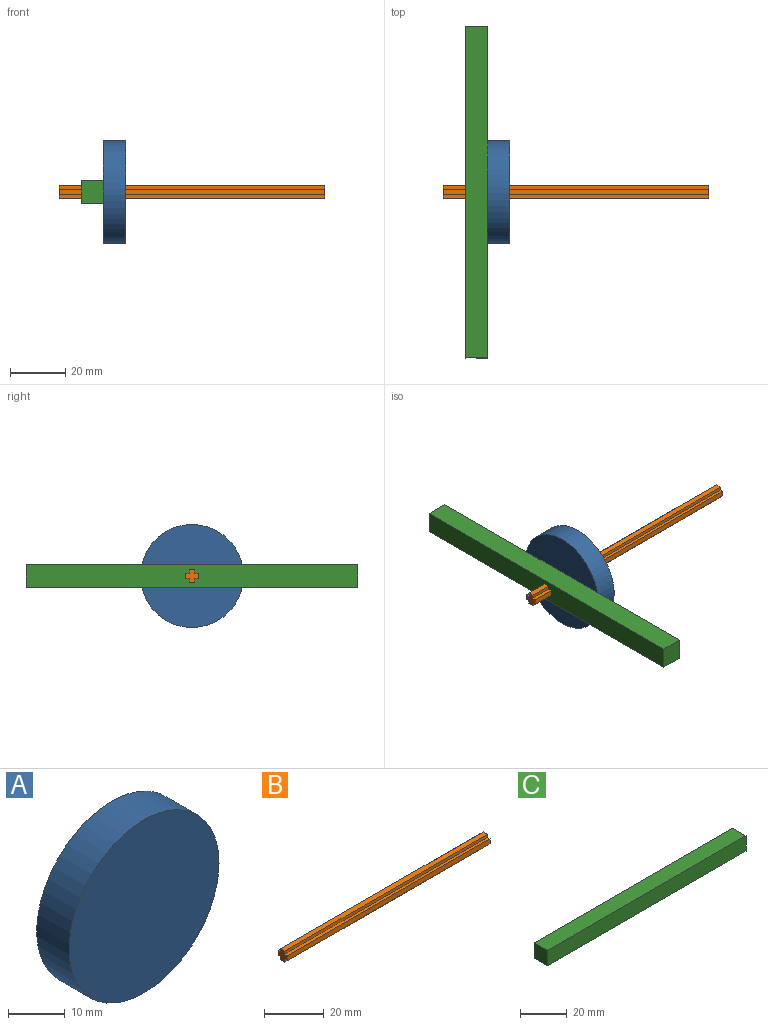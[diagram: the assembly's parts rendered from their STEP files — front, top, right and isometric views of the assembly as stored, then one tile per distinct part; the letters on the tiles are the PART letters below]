
ASSEMBLY  parts=3 mates=2
PART A: 3 faces, bbox 37.2x8x37.2 mm
  f0: cylinder r=18.6mm len=37.2mm, axis (0,1,0), area 934.9mm2, adj f1,f2
  f1: plane 37.2x37.2mm, normal (0,-1,0), area 1086.9mm2, adj f0
  f2: plane 37.2x37.2mm, normal (0,1,0), area 1086.9mm2, adj f0
PART B: 14 faces, bbox 96x4.5x4.5 mm
  f0: plane 4.5x4.5mm, normal (-1,0,0), area 14mm2, adj f2,f3,f4,f5,f6,f7,f8,f9
  f1: plane 4.5x4.5mm, normal (1,0,0), area 14mm2, adj f2,f3,f4,f5,f6,f7,f8,f9
  f2: plane 96x2mm, normal (0,0,1), area 192mm2, adj f0,f1,f3,f13
  f3: plane 96x1.25mm, normal (0,-1,0), area 120mm2, adj f0,f1,f2,f4
  f4: plane 96x1.25mm, normal (0,0,1), area 120mm2, adj f0,f1,f3,f5
  f5: plane 96x2mm, normal (0,-1,0), area 192mm2, adj f0,f1,f4,f6
  f6: plane 96x1.25mm, normal (0,0,-1), area 120mm2, adj f0,f1,f5,f7
  f7: plane 96x1.25mm, normal (0,-1,0), area 120mm2, adj f0,f1,f6,f8
  f8: plane 96x2mm, normal (0,0,-1), area 192mm2, adj f0,f1,f7,f9
  f9: plane 96x1.25mm, normal (0,1,0), area 120mm2, adj f0,f1,f8,f10
  f10: plane 96x1.25mm, normal (0,0,-1), area 120mm2, adj f0,f1,f9,f11
  f11: plane 96x2mm, normal (0,1,0), area 192mm2, adj f0,f1,f10,f12
  f12: plane 96x1.25mm, normal (0,0,1), area 120mm2, adj f0,f1,f11,f13
  f13: plane 96x1.25mm, normal (0,1,0), area 120mm2, adj f0,f1,f2,f12
PART C: 6 faces, bbox 120x8x8 mm
  f0: plane 120x8mm, normal (0,0,-1), area 960mm2, adj f1,f3,f4,f5
  f1: plane 8x8mm, normal (1,0,0), area 64mm2, adj f0,f2,f4,f5
  f2: plane 120x8mm, normal (0,0,1), area 960mm2, adj f1,f3,f4,f5
  f3: plane 8x8mm, normal (-1,0,0), area 64mm2, adj f0,f2,f4,f5
  f4: plane 120x8mm, normal (0,-1,0), area 960mm2, adj f0,f1,f2,f3
  f5: plane 120x8mm, normal (0,1,0), area 960mm2, adj f0,f1,f2,f3
PLACE A rot(axis=(0,0,1),90deg) t=(-3.73,-14.44,-23.44)mm
PLACE B t=(24.27,-14.44,-23.44)mm
PLACE C rot(axis=(0,0,-1),90deg) t=(-11.73,-14.44,-27.44)mm
MATE fastened A.f0 <-> C.f5  axis (-1,0,0) through (-7.73,-14.44,-23.44)mm
MATE slider B.f1 <-> A.f0  axis (1,0,0) through (72.27,-14.44,-23.44)mm
